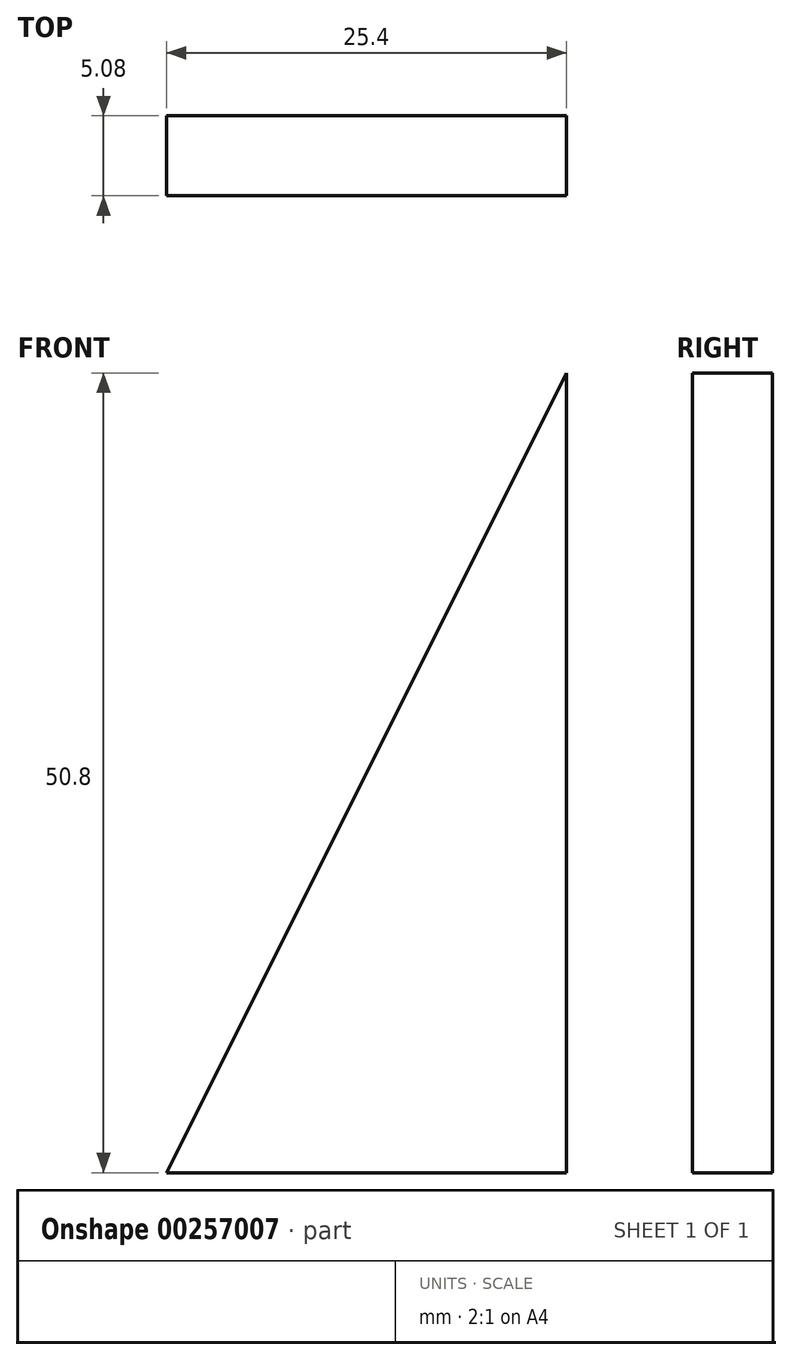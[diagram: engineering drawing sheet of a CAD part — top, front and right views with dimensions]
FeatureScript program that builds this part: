
annotation { "Feature Type Name" : "Feature", "Feature Type Description" : "" }
export const myFeature = defineFeature(function(context is Context, id is Id, definition is map)
    precondition{}
    {
        {
            var Q0;
            Q0=qCreatedBy(makeId("Front.planeOp"),FACE);
            var sketch = newSketch(context, id + "F0", { "sketchPlane" : qUnion([Q0])});
            skLineSegment(sketch, "E0", {"start": v(0, 0) * mm, "end": v(0, 50.8) * mm});
            skLineSegment(sketch, "E1", {"start": v(0, 50.8) * mm, "end": v(-25.4, 0) * mm});
            skLineSegment(sketch, "E2", {"start": v(-25.4, 0) * mm, "end": v(0, 0) * mm});
            skSolve(sketch);
        }
        {
            var Q0;
            Q0=makeQuery(id+"F0.imprint","IMPRINT",FACE,{"disambiguationData":[TD([[makeQuery(id+"F0.imprint","IMPRINT",EDGE,{"derivedFrom":sQuery(id+"F0.wireOp",EDGE,"E0")}),1.0]])]});
            extrude(context, id + "F1", {"entities" : qUnion([Q0]), "depth" : 5.08 * mm});
        }
    });
